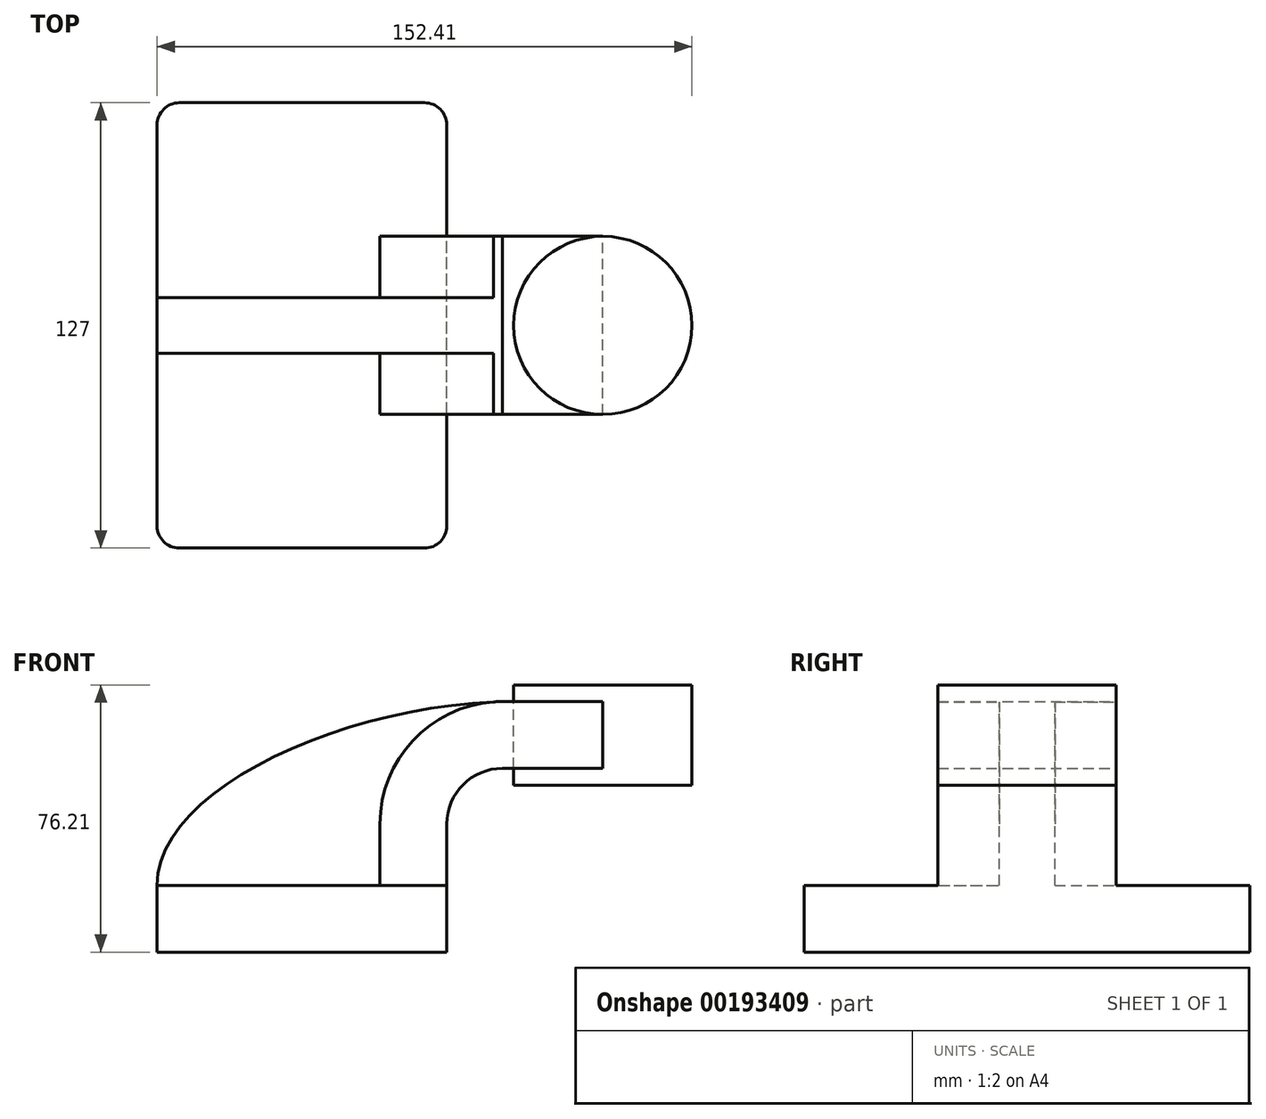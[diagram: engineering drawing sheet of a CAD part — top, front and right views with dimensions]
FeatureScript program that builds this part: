
annotation { "Feature Type Name" : "Feature", "Feature Type Description" : "" }
export const myFeature = defineFeature(function(context is Context, id is Id, definition is map)
    precondition{}
    {
        {
            var Q0;
            Q0=qCreatedBy(makeId("Front.planeOp"),FACE);
            var sketch = newSketch(context, id + "F0", { "sketchPlane" : qUnion([Q0])});
            skLineSegment(sketch, "E0.bottom", {"start": v(-41.28, 9.52) * mm, "end": v(41.27, 9.53) * mm});
            skLineSegment(sketch, "E0.top", {"start": v(-41.28, -9.53) * mm, "end": v(41.28, -9.53) * mm});
            skLineSegment(sketch, "E0.left", {"start": v(-41.28, 9.52) * mm, "end": v(-41.28, -9.53) * mm});
            skLineSegment(sketch, "E0.right", {"start": v(41.27, 9.53) * mm, "end": v(41.28, -9.52) * mm});
            skPoint(sketch, "E0.middle", {"position": v(0, 0) * mm});
            skLineSegment(sketch, "E1.bottom", {"start": v(60.33, 38.1) * mm, "end": v(111.13, 38.1) * mm});
            skLineSegment(sketch, "E1.top", {"start": v(60.33, 66.67) * mm, "end": v(111.13, 66.67) * mm});
            skLineSegment(sketch, "E1.left", {"start": v(60.33, 38.1) * mm, "end": v(60.33, 66.67) * mm});
            skLineSegment(sketch, "E1.right", {"start": v(111.13, 38.1) * mm, "end": v(111.13, 66.67) * mm});
            skPoint(sketch, "E1.middle", {"position": v(85.73, 52.39) * mm});
            skLineSegment(sketch, "E2", {"start": v(41.27, 9.53) * mm, "end": v(41.27, 27) * mm});
            skArc(sketch, "E3", {"start": v(41.27, 27) * mm, "mid": v(45.92, 38.23) * mm, "end": v(57.15, 42.88) * mm});
            skLineSegment(sketch, "E4", {"start": v(57.15, 42.88) * mm, "end": v(85.73, 42.88) * mm});
            skLineSegment(sketch, "E5.0", {"start": v(57.15, 61.93) * mm, "end": v(85.73, 61.93) * mm});
            skArc(sketch, "E5.1", {"start": v(22.22, 27) * mm, "mid": v(32.45, 51.7) * mm, "end": v(57.15, 61.93) * mm});
            skLineSegment(sketch, "E5.2", {"start": v(22.22, 9.53) * mm, "end": v(22.22, 27) * mm});
            skFitSpline(sketch, "E6", {"points": [v(-41.28, 9.53) * mm, v(57.15, 61.93) * mm], "startDerivative": vector(-0.32, 81.64) * mm, "endDerivative": vector(138.51, 3.77) * mm});
            skLineSegment(sketch, "E7", {"start": v(85.73, 61.93) * mm, "end": v(85.73, 42.88) * mm});
            skLineSegment(sketch, "E8", {"start": v(85.72, 61.93) * mm, "end": v(85.72, 66.67) * mm});
            skLineSegment(sketch, "E9", {"start": v(85.73, 66.67) * mm, "end": v(85.73, 38.1) * mm});
            skLineSegment(sketch, "E10", {"start": v(85.72, 38.1) * mm, "end": v(85.72, 42.88) * mm});
            skSolve(sketch);
        }
        {
            var Q0;
            Q0=makeQuery(id+"F0.imprint","IMPRINT",FACE,{"disambiguationData":[TD([[makeQuery(id+"F0.imprint","IMPRINT",EDGE,{"derivedFrom":sQuery(id+"F0.wireOp",EDGE,"E0.top")}),1.0]])]});
            extrude(context, id + "F1", {"entities" : qUnion([Q0]), "endBound" : BoundingType.SYMMETRIC, "depth" : 127 * mm});
        }
        {
            var Q0;
            {var subQ1=sQuery(id+"F0.wireOp",EDGE,"E2");Q0=makeQuery(id+"F0.imprint","IMPRINT",FACE,{"disambiguationData":[TD([[makeQuery(id+"F0.imprint","IMPRINT",EDGE,{"derivedFrom":subQ1}),1.0]])]});}
            var Q1;
            {var subQ5=sQuery(id+"F0.wireOp",EDGE,"E7");Q1=makeQuery(id+"F0.imprint","IMPRINT",FACE,{"disambiguationData":[TD([[makeQuery(id+"F0.imprint","IMPRINT",EDGE,{"derivedFrom":subQ5}),-1.0]])]});}
            var Q2;
            {var subQ0=sQuery(id+"F0.wireOp",EDGE,"E4");var subQ1=sQuery(id+"F0.wireOp",EDGE,"E1.left");var subQ2=makeQuery(id+"F0.imprint","INTERSECT",VERTEX,{"derivedFrom":[subQ1,subQ0]});Q2=makeQuery(id+"F0.imprint","IMPRINT",FACE,{"disambiguationData":[TD([[makeQuery(id+"F0.imprint","IMPRINT",EDGE,{"disambiguationData":[TD([[subQ2,-1.0]])],"derivedFrom":subQ1}),-1.0]])]});}
            extrude(context, id + "F2", {"entities" : qUnion([Q0, Q1, Q2]), "operationType" : NewBodyOperationType.ADD, "endBound" : BoundingType.SYMMETRIC, "depth" : 50.8 * mm});
        }
        {
            var Q0;
            {var subQ3=sQuery(id+"F0.wireOp",EDGE,"E5.2");Q0=makeQuery(id+"F0.imprint","IMPRINT",FACE,{"disambiguationData":[TD([[makeQuery(id+"F0.imprint","IMPRINT",EDGE,{"derivedFrom":subQ3}),1.0]])]});}
            extrude(context, id + "F3", {"entities" : qUnion([Q0]), "operationType" : NewBodyOperationType.ADD, "endBound" : BoundingType.SYMMETRIC, "depth" : 15.88 * mm});
        }
        {
            var Q0;
            {var subQ0=sQuery(id+"F0.wireOp",EDGE,"E1.right");Q0=makeQuery(id+"F0.imprint","IMPRINT",FACE,{"disambiguationData":[TD([[makeQuery(id+"F0.imprint","IMPRINT",EDGE,{"derivedFrom":subQ0}),1.0]])]});}
            var Q1;
            Q1=sQuery(id+"F0.wireOp",EDGE,"E7");
            revolve(context, id + "F4", {"entities" : qUnion([Q0]), "axis" : qUnion([Q1]), "revolveType" : RevolveType.FULL});
        }
        {
            var Q0;
            Q0=makeQuery(id+"F1.opExtrude","CAP_EDGE",EDGE,{"disambiguationData":[OSD([sQuery(id+"F0.wireOp",EDGE,"E0.right")])],"isStart":false});
            var Q1;
            Q1=makeQuery(id+"F1.opExtrude","CAP_EDGE",EDGE,{"disambiguationData":[OSD([sQuery(id+"F0.wireOp",EDGE,"E0.left")])],"isStart":false});
            var Q2;
            Q2=makeQuery(id+"F1.opExtrude","CAP_EDGE",EDGE,{"disambiguationData":[OSD([sQuery(id+"F0.wireOp",EDGE,"E0.left")])],"isStart":true});
            var Q3;
            Q3=makeQuery(id+"F1.opExtrude","CAP_EDGE",EDGE,{"disambiguationData":[OSD([sQuery(id+"F0.wireOp",EDGE,"E0.right")])],"isStart":true});
            fillet(context, id + "F5", {"entities" : qUnion([Q0, Q1, Q2, Q3]), "radius" : 6.35 * mm, "tangentPropagation" : true, "allowEdgeOverflow" : false});
        }
    });
